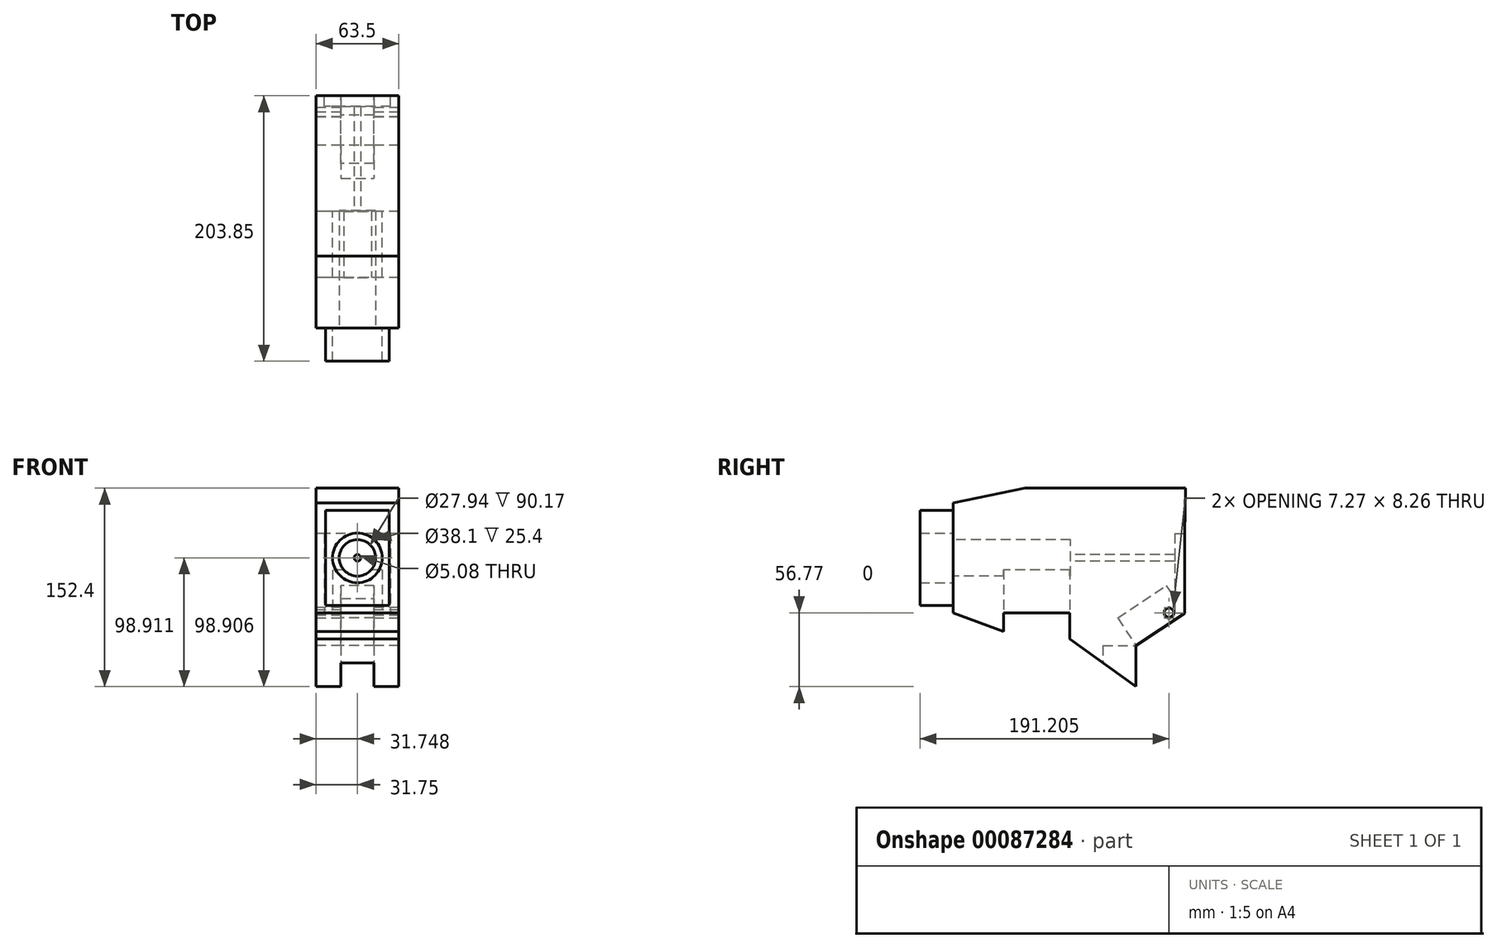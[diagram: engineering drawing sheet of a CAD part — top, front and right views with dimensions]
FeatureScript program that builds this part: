
annotation { "Feature Type Name" : "Feature", "Feature Type Description" : "" }
export const myFeature = defineFeature(function(context is Context, id is Id, definition is map)
    precondition{}
    {
        {
            var Q0;
            Q0=qCreatedBy(makeId("Right.planeOp"),FACE);
            var sketch = newSketch(context, id + "F0", { "sketchPlane" : qUnion([Q0])});
            skLineSegment(sketch, "E0", {"start": v(88.06, 60.78) * mm, "end": v(88.06, -0.34) * mm});
            skLineSegment(sketch, "E1", {"start": v(88.06, -0.34) * mm, "end": v(50.8, -25.2) * mm});
            skLineSegment(sketch, "E2", {"start": v(50.8, -25.2) * mm, "end": v(50.8, -56.77) * mm});
            skLineSegment(sketch, "E3", {"start": v(50.8, -56.77) * mm, "end": v(0, -20.1) * mm});
            skLineSegment(sketch, "E4", {"start": v(0, -20.1) * mm, "end": v(0, 0) * mm});
            skLineSegment(sketch, "E5", {"start": v(0, 0) * mm, "end": v(-50.8, 0) * mm});
            skLineSegment(sketch, "E6", {"start": v(-50.8, 0) * mm, "end": v(-50.8, -14.5) * mm});
            skLineSegment(sketch, "E7", {"start": v(-50.8, -14.5) * mm, "end": v(-89.74, 0) * mm});
            skLineSegment(sketch, "E8", {"start": v(-89.74, 0) * mm, "end": v(-89.74, 84.27) * mm});
            skLineSegment(sketch, "E9", {"start": v(-89.74, 84.27) * mm, "end": v(-34.44, 95.63) * mm});
            skLineSegment(sketch, "E10", {"start": v(-34.44, 95.63) * mm, "end": v(88.7, 95.63) * mm});
            skLineSegment(sketch, "E11", {"start": v(88.7, 95.63) * mm, "end": v(88.06, 60.78) * mm});
            skCircle(sketch, "E12.cCircle", {"center": v(76.07, 0) * mm, "radius": 3.58 * mm, "construction": true});
            skLineSegment(sketch, "E12.0", {"start": v(72.43, 1.97) * mm, "end": v(75.95, 4.13) * mm});
            skLineSegment(sketch, "E12.1", {"start": v(75.95, 4.13) * mm, "end": v(79.58, 2.16) * mm});
            skLineSegment(sketch, "E12.2", {"start": v(79.58, 2.16) * mm, "end": v(79.7, -1.97) * mm});
            skLineSegment(sketch, "E12.3", {"start": v(79.7, -1.97) * mm, "end": v(76.18, -4.13) * mm});
            skLineSegment(sketch, "E12.4", {"start": v(76.18, -4.13) * mm, "end": v(72.55, -2.16) * mm});
            skLineSegment(sketch, "E12.5", {"start": v(72.55, -2.16) * mm, "end": v(72.43, 1.97) * mm});
            skPoint(sketch, "E12.0.midPoint", {"position": v(74.2, 3.05) * mm});
            skSolve(sketch);
        }
        {
            var Q0;
            Q0 = qSketchRegion(id + "F0", true);
            extrude(context, id + "F1", {"entities" : qUnion([Q0]), "depth" : 63.5 * mm});
        }
        {
            var Q0;
            Q0=makeQuery(id+"F1.opExtrude","SWEPT_FACE",FACE,{"disambiguationData":[OSD([sQuery(id+"F0.wireOp",EDGE,"E1")])]});
            var sketch = newSketch(context, id + "F2", { "sketchPlane" : qUnion([Q0])});
            skLineSegment(sketch, "E13.bottom", {"start": v(19.05, -28.26) * mm, "end": v(44.45, -28.26) * mm});
            skLineSegment(sketch, "E13.top", {"start": v(19.05, -73.06) * mm, "end": v(44.45, -73.06) * mm});
            skLineSegment(sketch, "E13.left", {"start": v(19.05, -28.26) * mm, "end": v(19.05, -73.06) * mm});
            skLineSegment(sketch, "E13.right", {"start": v(44.45, -28.26) * mm, "end": v(44.45, -73.06) * mm});
            skPoint(sketch, "E13.middle", {"position": v(31.75, -50.66) * mm});
            skPoint(sketch, "E13.middle.positionSnap0", {"position": v(0, -50.66) * mm});
            skPoint(sketch, "E13.middle.positionSnap1", {"position": v(31.75, -73.06) * mm});
            skPoint(sketch, "E13.centerSnap0", {"position": v(0, -50.66) * mm});
            skPoint(sketch, "E13.centerSnap1", {"position": v(31.75, -73.06) * mm});
            skSolve(sketch);
        }
        {
            var Q0;
            Q0 = qSketchRegion(id + "F2", true);
            extrude(context, id + "F3", {"entities" : qUnion([Q0]), "operationType" : NewBodyOperationType.REMOVE, "oppositeDirection" : true, "depth" : 25.4 * mm});
        }
        {
            var Q0;
            Q0=makeQuery(id+"F1.opExtrude","SWEPT_FACE",FACE,{"disambiguationData":[OSD([sQuery(id+"F0.wireOp",EDGE,"E2")])]});
            var sketch = newSketch(context, id + "F4", { "sketchPlane" : qUnion([Q0])});
            skLineSegment(sketch, "E14.bottom", {"start": v(-19.05, -25.2) * mm, "end": v(-44.45, -25.2) * mm});
            skLineSegment(sketch, "E14.top", {"start": v(-19.05, -56.77) * mm, "end": v(-44.45, -56.77) * mm});
            skLineSegment(sketch, "E14.left", {"start": v(-19.05, -25.2) * mm, "end": v(-19.05, -56.77) * mm});
            skLineSegment(sketch, "E14.right", {"start": v(-44.45, -25.2) * mm, "end": v(-44.45, -56.77) * mm});
            skPoint(sketch, "E14.middle", {"position": v(-31.75, -40.99) * mm});
            skPoint(sketch, "E14.middle.positionSnap0", {"position": v(0, -40.99) * mm});
            skPoint(sketch, "E14.middle.positionSnap1", {"position": v(-31.75, -25.2) * mm});
            skPoint(sketch, "E14.centerSnap0", {"position": v(0, -40.99) * mm});
            skPoint(sketch, "E14.centerSnap1", {"position": v(-31.75, -25.2) * mm});
            skSolve(sketch);
        }
        {
            var Q0;
            Q0 = qSketchRegion(id + "F4", true);
            extrude(context, id + "F5", {"entities" : qUnion([Q0]), "operationType" : NewBodyOperationType.REMOVE, "oppositeDirection" : true, "depth" : 25.4 * mm});
        }
        {
            var Q0;
            Q0=makeQuery(id+"F1.opExtrude","SWEPT_FACE",FACE,{"disambiguationData":[OSD([sQuery(id+"F0.wireOp",EDGE,"E8")])]});
            var sketch = newSketch(context, id + "F6", { "sketchPlane" : qUnion([Q0])});
            skCircle(sketch, "E15", {"center": v(31.75, 42.14) * mm, "radius": 19.05 * mm});
            skPoint(sketch, "E15.centerSnap0", {"position": v(63.5, 42.14) * mm});
            skPoint(sketch, "E15.centerSnap1", {"position": v(31.75, 84.27) * mm});
            skCircle(sketch, "E16", {"center": v(31.75, 42.14) * mm, "radius": 13.97 * mm});
            skLineSegment(sketch, "E17.bottom", {"start": v(56.16, 78.58) * mm, "end": v(7.34, 78.58) * mm});
            skLineSegment(sketch, "E17.top", {"start": v(56.16, 5.7) * mm, "end": v(7.34, 5.7) * mm});
            skLineSegment(sketch, "E17.left", {"start": v(56.16, 78.58) * mm, "end": v(56.16, 5.7) * mm});
            skLineSegment(sketch, "E17.right", {"start": v(7.34, 78.58) * mm, "end": v(7.34, 5.7) * mm});
            skSolve(sketch);
        }
        {
            var Q0;
            Q0 = qSketchRegion(id + "F6", true);
            extrude(context, id + "F7", {"entities" : qUnion([Q0]), "operationType" : NewBodyOperationType.ADD, "depth" : 25.4 * mm});
        }
        {
            var Q0;
            Q0=makeQuery(id+"F6.imprint","IMPRINT",FACE,{"disambiguationData":[TD([[makeQuery(id+"F6.imprint","IMPRINT",EDGE,{"derivedFrom":sQuery(id+"F6.wireOp",EDGE,"E16")}),1.0]])]});
            extrude(context, id + "F8", {"entities" : qUnion([Q0]), "operationType" : NewBodyOperationType.REMOVE, "oppositeDirection" : true, "depth" : 90.17 * mm});
        }
        {
            var Q0;
            Q0=makeQuery(id+"F1.opExtrude","SWEPT_FACE",FACE,{"disambiguationData":[OSD([sQuery(id+"F0.wireOp",EDGE,"E5")])]});
            var sketch = newSketch(context, id + "F9", { "sketchPlane" : qUnion([Q0])});
            skLineSegment(sketch, "E18.bottom", {"start": v(50.8, 50.8) * mm, "end": v(12.7, 50.8) * mm});
            skLineSegment(sketch, "E18.top", {"start": v(50.8, 0) * mm, "end": v(12.7, 0) * mm});
            skLineSegment(sketch, "E18.left", {"start": v(50.8, 50.8) * mm, "end": v(50.8, 0) * mm});
            skLineSegment(sketch, "E18.right", {"start": v(12.7, 50.8) * mm, "end": v(12.7, 0) * mm});
            skPoint(sketch, "E18.middle", {"position": v(31.75, 25.4) * mm});
            skPoint(sketch, "E18.middle.positionSnap0", {"position": v(31.75, 50.8) * mm});
            skPoint(sketch, "E18.middle.positionSnap1", {"position": v(63.5, 25.4) * mm});
            skPoint(sketch, "E18.centerSnap0", {"position": v(31.75, 50.8) * mm});
            skPoint(sketch, "E18.centerSnap1", {"position": v(63.5, 25.4) * mm});
            skSolve(sketch);
        }
        {
            var Q0;
            Q0 = qSketchRegion(id + "F9", true);
            extrude(context, id + "F10", {"entities" : qUnion([Q0]), "operationType" : NewBodyOperationType.REMOVE, "oppositeDirection" : true, "depth" : 33.02 * mm});
        }
        {
            var Q0;
            Q0=makeQuery(id+"F1.opExtrude","SWEPT_FACE",FACE,{"disambiguationData":[OSD([sQuery(id+"F0.wireOp",EDGE,"E0")])]});
            var sketch = newSketch(context, id + "F11", { "sketchPlane" : qUnion([Q0])});
            skLineSegment(sketch, "E19.bottom", {"start": v(-6.35, 60.78) * mm, "end": v(-57.15, 60.78) * mm});
            skLineSegment(sketch, "E19.top", {"start": v(-6.35, -0.34) * mm, "end": v(-57.15, -0.34) * mm});
            skLineSegment(sketch, "E19.left", {"start": v(-6.35, 60.78) * mm, "end": v(-6.35, -0.34) * mm});
            skLineSegment(sketch, "E19.right", {"start": v(-57.15, 60.78) * mm, "end": v(-57.15, -0.34) * mm});
            skPoint(sketch, "E19.middle", {"position": v(-31.75, 30.22) * mm});
            skPoint(sketch, "E19.middle.positionSnap0", {"position": v(-31.75, 60.78) * mm});
            skPoint(sketch, "E19.middle.positionSnap1", {"position": v(0, 30.22) * mm});
            skPoint(sketch, "E19.centerSnap0", {"position": v(-31.75, 60.78) * mm});
            skPoint(sketch, "E19.centerSnap1", {"position": v(0, 30.22) * mm});
            skSolve(sketch);
        }
        {
            var Q0;
            Q0 = qSketchRegion(id + "F11", true);
            extrude(context, id + "F12", {"entities" : qUnion([Q0]), "operationType" : NewBodyOperationType.REMOVE, "oppositeDirection" : true, "depth" : 7.62 * mm});
        }
        {
            var Q0;
            Q0=makeQuery(id+"F6.imprint","IMPRINT",FACE,{"disambiguationData":[TD([[makeQuery(id+"F6.imprint","IMPRINT",EDGE,{"derivedFrom":sQuery(id+"F6.wireOp",EDGE,"E16")}),1.0]])]});
            var sketch = newSketch(context, id + "F13", { "sketchPlane" : qUnion([Q0])});
            skCircle(sketch, "E20", {"center": v(31.75, 42.14) * mm, "radius": 2.54 * mm});
            skSolve(sketch);
        }
        {
            var Q0;
            Q0 = qSketchRegion(id + "F13", true);
            extrude(context, id + "F14", {"entities" : qUnion([Q0]), "operationType" : NewBodyOperationType.REMOVE, "oppositeDirection" : true, "depth" : 584.2 * mm});
        }
    });
